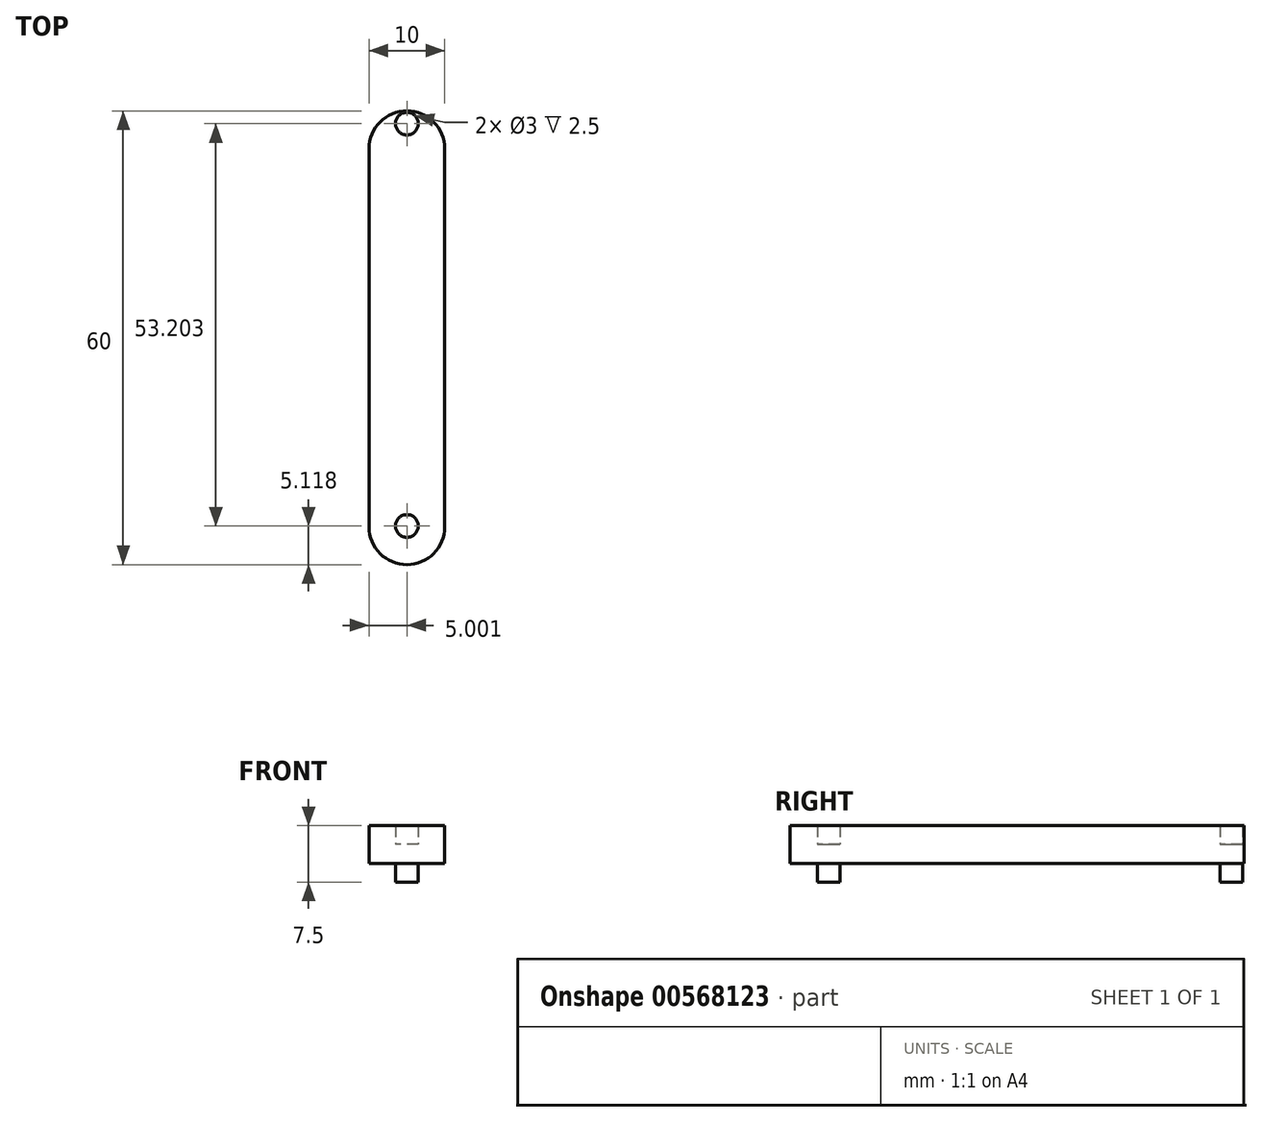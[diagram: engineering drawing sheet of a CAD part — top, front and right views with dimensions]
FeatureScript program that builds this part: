
annotation { "Feature Type Name" : "Feature", "Feature Type Description" : "" }
export const myFeature = defineFeature(function(context is Context, id is Id, definition is map)
    precondition{}
    {
        {
            var Q0;
            Q0=qCreatedBy(makeId("Top.planeOp"),FACE);
            var sketch = newSketch(context, id + "F0", { "sketchPlane" : qUnion([Q0])});
            skLineSegment(sketch, "E0.bottom", {"start": v(-37.8, 51) * mm, "end": v(-27.8, 51) * mm});
            skLineSegment(sketch, "E0.top", {"start": v(-37.8, -9) * mm, "end": v(-27.8, -9) * mm});
            skLineSegment(sketch, "E0.left", {"start": v(-37.8, 51) * mm, "end": v(-37.8, -9) * mm});
            skLineSegment(sketch, "E0.right", {"start": v(-27.8, 51) * mm, "end": v(-27.8, -9) * mm});
            skCircle(sketch, "E1", {"center": v(-32.8, 49.31) * mm, "radius": 1.5 * mm});
            skPoint(sketch, "E1.centerSnap0", {"position": v(-32.8, 51) * mm});
            skCircle(sketch, "E2", {"center": v(-32.8, -3.9) * mm, "radius": 1.5 * mm});
            skSolve(sketch);
        }
        {
            var Q0;
            Q0=makeQuery(id+"F0.imprint","IMPRINT",FACE,{"disambiguationData":[TD([[makeQuery(id+"F0.imprint","IMPRINT",EDGE,{"derivedFrom":sQuery(id+"F0.wireOp",EDGE,"E0.bottom")}),-1.0]])]});
            extrude(context, id + "F1", {"entities" : qUnion([Q0]), "endBound" : BoundingType.SYMMETRIC, "depth" : 5 * mm, "offsetDistance" : 25 * mm});
        }
        {
            var Q0;
            Q0=makeQuery(id+"F0.imprint","IMPRINT",FACE,{"disambiguationData":[TD([[makeQuery(id+"F0.imprint","IMPRINT",EDGE,{"derivedFrom":sQuery(id+"F0.wireOp",EDGE,"E1")}),1.0]])]});
            var Q1;
            Q1=makeQuery(id+"F0.imprint","IMPRINT",FACE,{"disambiguationData":[TD([[makeQuery(id+"F0.imprint","IMPRINT",EDGE,{"derivedFrom":sQuery(id+"F0.wireOp",EDGE,"E2")}),1.0]])]});
            extrude(context, id + "F2", {"entities" : qUnion([Q0, Q1]), "operationType" : NewBodyOperationType.ADD, "oppositeDirection" : true, "depth" : 5 * mm, "offsetDistance" : 25 * mm});
        }
        {
            var Q0;
            Q0=makeQuery(id+"F1.opExtrude","SWEPT_EDGE",EDGE,{"disambiguationData":[OSD([sQuery(id+"F0.wireOp",EDGE,"E0.bottom"),sQuery(id+"F0.wireOp",EDGE,"E0.right")])]});
            var Q1;
            Q1=makeQuery(id+"F1.opExtrude","SWEPT_EDGE",EDGE,{"disambiguationData":[OSD([sQuery(id+"F0.wireOp",EDGE,"E0.bottom"),sQuery(id+"F0.wireOp",EDGE,"E0.left")])]});
            var Q2;
            Q2=makeQuery(id+"F1.opExtrude","SWEPT_EDGE",EDGE,{"disambiguationData":[OSD([sQuery(id+"F0.wireOp",EDGE,"E0.top"),sQuery(id+"F0.wireOp",EDGE,"E0.right")])]});
            var Q3;
            Q3=makeQuery(id+"F1.opExtrude","SWEPT_EDGE",EDGE,{"disambiguationData":[OSD([sQuery(id+"F0.wireOp",EDGE,"E0.top"),sQuery(id+"F0.wireOp",EDGE,"E0.left")])]});
            fillet(context, id + "F3", {"entities" : qUnion([Q0, Q1, Q2, Q3]), "radius" : 5 * mm, "tangentPropagation" : true, "allowEdgeOverflow" : false});
        }
    });
